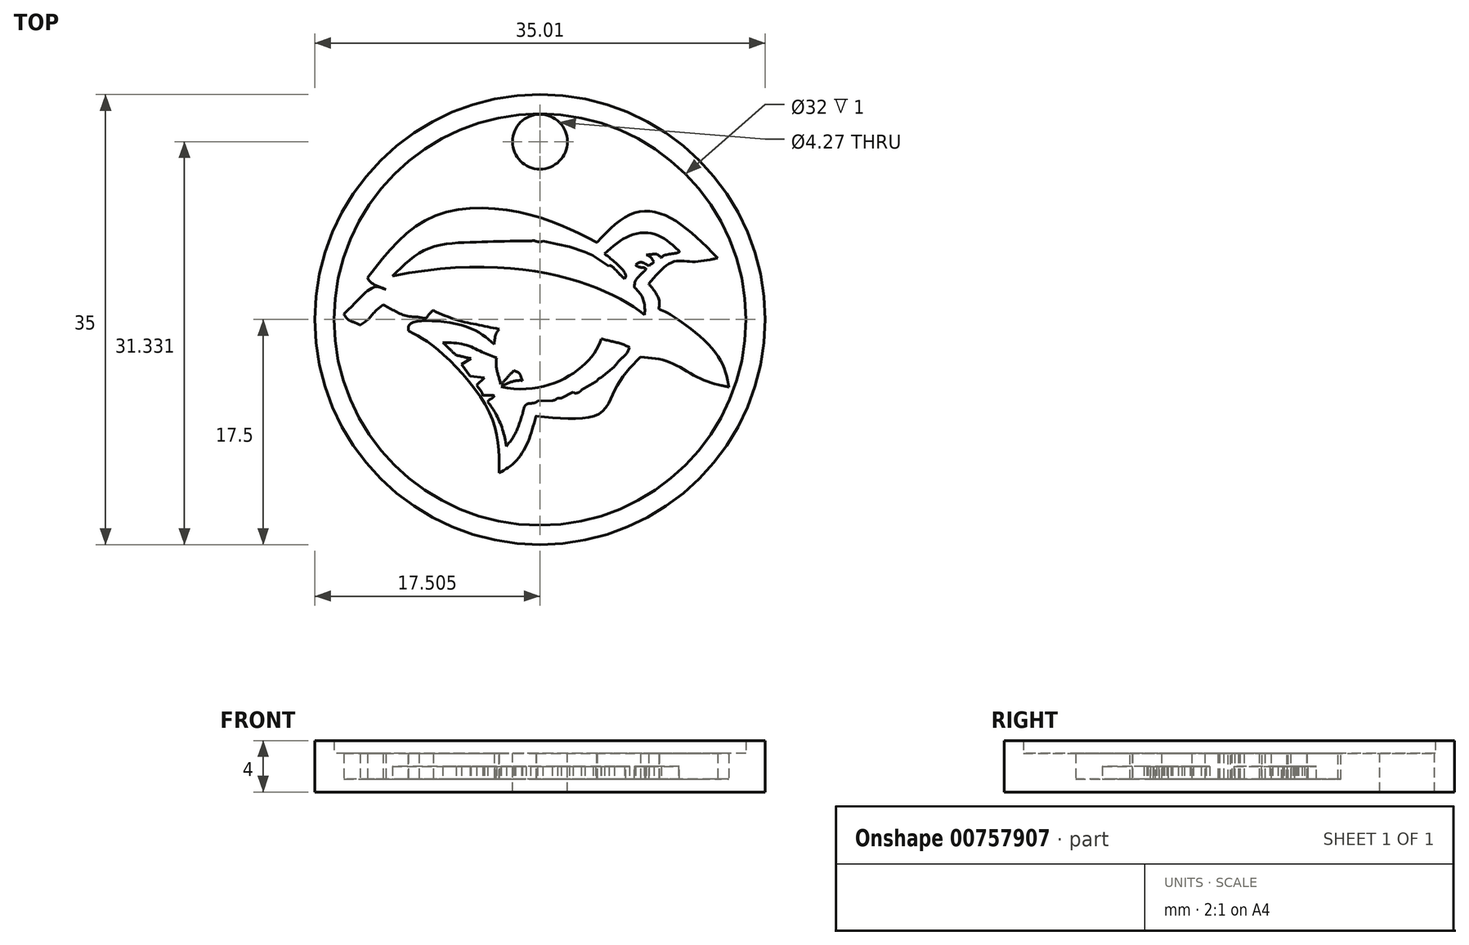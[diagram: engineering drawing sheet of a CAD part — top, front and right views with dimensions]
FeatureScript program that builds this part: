
annotation { "Feature Type Name" : "Feature", "Feature Type Description" : "" }
export const myFeature = defineFeature(function(context is Context, id is Id, definition is map)
    precondition{}
    {
        {
            var Q0;
            Q0=qCreatedBy(makeId("Top.planeOp"),FACE);
            var sketch = newSketch(context, id + "F0", { "sketchPlane" : qUnion([Q0])});
            skFitSpline(sketch, "E0", {"points": [v(1.9, -11.18) * mm, v(19.73, -8.42) * mm], "startDerivative": vector(15.68, 14.44) * mm, "endDerivative": vector(15.49, -6.43) * mm});
            skFitSpline(sketch, "E1", {"points": [v(19.73, -8.42) * mm, v(29.13, -9.64) * mm], "startDerivative": vector(8.75, 6.87) * mm, "endDerivative": vector(11.03, -9.35) * mm});
            skFitSpline(sketch, "E2", {"points": [v(29.13, -9.64) * mm, v(23.76, -11.66) * mm], "startDerivative": vector(-5.82, -0.85) * mm, "endDerivative": vector(-5.7, -5.15) * mm});
            skFitSpline(sketch, "E3", {"points": [v(23.76, -11.66) * mm, v(24.55, -13.61) * mm], "startDerivative": vector(0.88, -1.03) * mm, "endDerivative": vector(0, -2.22) * mm});
            skFitSpline(sketch, "E4", {"points": [v(24.55, -13.61) * mm, v(30, -19.69) * mm], "startDerivative": vector(2.55, -1.23) * mm, "endDerivative": vector(3.23, -8.18) * mm});
            skFitSpline(sketch, "E5", {"points": [v(30, -19.69) * mm, v(23.14, -17.33) * mm], "startDerivative": vector(-6.71, 1.98) * mm, "endDerivative": vector(-6.91, 1.31) * mm});
            skFitSpline(sketch, "E6", {"points": [v(23.14, -17.33) * mm, v(15, -21.93) * mm], "startDerivative": vector(-5.52, -6.77) * mm, "endDerivative": vector(-14.9, -0.63) * mm});
            skFitSpline(sketch, "E7", {"points": [v(1.9, -11.18) * mm, v(3.35, -12.11) * mm], "startDerivative": vector(1, -1.24) * mm, "endDerivative": vector(1.42, -0.66) * mm});
            skFitSpline(sketch, "E8", {"points": [v(3.35, -12.11) * mm, v(0.08, -14.01) * mm], "startDerivative": vector(-2.7, 0.63) * mm, "endDerivative": vector(-3.03, -3.02) * mm});
            skFitSpline(sketch, "E9", {"points": [v(0.08, -14.01) * mm, v(1.36, -14.87) * mm], "startDerivative": vector(1.17, -1.4) * mm, "endDerivative": vector(1.26, -0.62) * mm});
            skFitSpline(sketch, "E10", {"points": [v(1.36, -14.87) * mm, v(3.14, -13.28) * mm], "startDerivative": vector(2.06, 1.6) * mm, "endDerivative": vector(1.79, 1.42) * mm});
            skFitSpline(sketch, "E11", {"points": [v(3.14, -13.28) * mm, v(5.92, -14.25) * mm], "startDerivative": vector(2.61, -1.42) * mm, "endDerivative": vector(3, -0.33) * mm});
            skFitSpline(sketch, "E12", {"points": [v(5.92, -14.25) * mm, v(7.02, -13.73) * mm], "startDerivative": vector(1.6, -0.17) * mm, "endDerivative": vector(0.88, 0.76) * mm});
            skFitSpline(sketch, "E13", {"points": [v(7.02, -13.73) * mm, v(12.14, -15.18) * mm], "startDerivative": vector(5.39, -2.15) * mm, "endDerivative": vector(4.98, -1.03) * mm});
            skFitSpline(sketch, "E14", {"points": [v(12.14, -15.18) * mm, v(11.76, -16.34) * mm], "startDerivative": vector(-0.68, -1.03) * mm, "endDerivative": vector(-0.16, -1.26) * mm});
            skFitSpline(sketch, "E15", {"points": [v(15, -21.93) * mm, v(12.15, -26.36) * mm], "startDerivative": vector(-1.92, -6.19) * mm, "endDerivative": vector(-3.55, -2.43) * mm});
            skFitSpline(sketch, "E16", {"points": [v(11.76, -16.34) * mm, v(5.1, -15.31) * mm], "startDerivative": vector(-7.02, 4.21) * mm, "endDerivative": vector(-0.52, -1.73) * mm});
            skFitSpline(sketch, "E17", {"points": [v(5.1, -15.31) * mm, v(12.15, -26.36) * mm], "startDerivative": vector(6.41, -4.03) * mm, "endDerivative": vector(2.12, -13.78) * mm});
            skArc(sketch, "E18.filletArc", {"start": v(1.99, -11.1) * mm, "mid": v(1.95, -11.19) * mm, "end": v(1.98, -11.27) * mm});
            skArc(sketch, "E19.filletArc", {"start": v(3.08, -12.09) * mm, "mid": v(3.12, -12.05) * mm, "end": v(3.1, -12) * mm});
            skArc(sketch, "E20.filletArc", {"start": v(3.2, -13.31) * mm, "mid": v(3.14, -13.3) * mm, "end": v(3.09, -13.33) * mm});
            skArc(sketch, "E21.filletArc", {"start": v(0.14, -13.94) * mm, "mid": v(0.11, -14.01) * mm, "end": v(0.14, -14.08) * mm});
            skArc(sketch, "E22.filletArc", {"start": v(1.3, -14.84) * mm, "mid": v(1.36, -14.85) * mm, "end": v(1.4, -14.83) * mm});
            skArc(sketch, "E23.filletArc", {"start": v(5.19, -15.2) * mm, "mid": v(5.15, -15.29) * mm, "end": v(5.2, -15.37) * mm});
            skArc(sketch, "E24.filletArc", {"start": v(12.12, -26.2) * mm, "mid": v(12.18, -26.28) * mm, "end": v(12.28, -26.27) * mm});
            skArc(sketch, "E25.filletArc", {"start": v(15.07, -21.92) * mm, "mid": v(15.01, -21.94) * mm, "end": v(14.98, -22) * mm});
            skArc(sketch, "E26.filletArc", {"start": v(23.2, -17.35) * mm, "mid": v(23.15, -17.35) * mm, "end": v(23.1, -17.38) * mm});
            skArc(sketch, "E27.filletArc", {"start": v(29.8, -19.63) * mm, "mid": v(29.9, -19.6) * mm, "end": v(29.92, -19.49) * mm});
            skArc(sketch, "E28.filletArc", {"start": v(24.55, -13.55) * mm, "mid": v(24.57, -13.6) * mm, "end": v(24.6, -13.64) * mm});
            skArc(sketch, "E29.filletArc", {"start": v(23.83, -11.6) * mm, "mid": v(23.8, -11.66) * mm, "end": v(23.82, -11.73) * mm});
            skArc(sketch, "E30.filletArc", {"start": v(28.9, -9.68) * mm, "mid": v(28.99, -9.6) * mm, "end": v(28.96, -9.5) * mm});
            skArc(sketch, "E31.filletArc", {"start": v(19.67, -8.4) * mm, "mid": v(19.72, -8.4) * mm, "end": v(19.77, -8.39) * mm});
            skFitSpline(sketch, "E32.0", {"points": [v(22.75, -17.02) * mm, v(22.29, -17.59) * mm, v(21.44, -18.7) * mm, v(20.04, -20.05) * mm, v(18.13, -21.04) * mm, v(16.19, -21.38) * mm, v(14.98, -21.43) * mm]});
            skArc(sketch, "E32.1", {"start": v(23.3, -16.85) * mm, "mid": v(22.98, -16.88) * mm, "end": v(22.71, -17.07) * mm});
            skFitSpline(sketch, "E32.2", {"points": [v(30.14, -19.2) * mm, v(29.06, -18.89) * mm, v(26.8, -17.94) * mm, v(24.44, -17.07) * mm, v(23.23, -16.84) * mm]});
            skFitSpline(sketch, "E32.3", {"points": [v(24.33, -14.06) * mm, v(24.37, -14.08) * mm, v(24.47, -14.13) * mm, v(24.77, -14.33) * mm, v(25.27, -14.71) * mm, v(26.02, -15.34) * mm, v(27.1, -16.37) * mm, v(28.5, -17.92) * mm, v(29.29, -19.25) * mm, v(29.53, -19.87) * mm]});
            skArc(sketch, "E32.4", {"start": v(24.05, -13.57) * mm, "mid": v(24.14, -13.87) * mm, "end": v(24.37, -14.08) * mm});
            skFitSpline(sketch, "E32.5", {"points": [v(20.04, -8.82) * mm, v(20.73, -8.27) * mm, v(21.74, -7.72) * mm, v(23.06, -7.44) * mm, v(24.07, -7.46) * mm, v(25.14, -7.72) * mm, v(26.65, -8.38) * mm, v(27.9, -9.26) * mm, v(28.8, -10.03) * mm]});
            skFitSpline(sketch, "E32.6", {"points": [v(29.06, -9.15) * mm, v(28.58, -9.22) * mm, v(27.66, -9.33) * mm, v(26.3, -9.59) * mm, v(24.9, -10.15) * mm, v(23.93, -10.84) * mm, v(23.43, -11.3) * mm]});
            skArc(sketch, "E32.7", {"start": v(23.5, -11.22) * mm, "mid": v(23.3, -11.62) * mm, "end": v(23.43, -12.04) * mm});
            skFitSpline(sketch, "E32.8", {"points": [v(23.38, -11.99) * mm, v(23.43, -12.05) * mm, v(23.58, -12.25) * mm, v(23.82, -12.69) * mm, v(24, -13.18) * mm, v(24.05, -13.48) * mm, v(24.05, -13.61) * mm]});
            skFitSpline(sketch, "E33", {"points": [v(12.44, -25.45) * mm, v(14.54, -21.9) * mm], "startDerivative": vector(2.73, 2.38) * mm, "endDerivative": vector(1.4, 4.03) * mm});
            skFitSpline(sketch, "E34", {"points": [v(14.54, -21.9) * mm, v(15.05, -21.42) * mm], "startDerivative": vector(0.26, 1.18) * mm, "endDerivative": vector(0.95, 0.12) * mm});
            skFitSpline(sketch, "E35", {"points": [v(12.44, -25.45) * mm, v(6.55, -15.62) * mm], "startDerivative": vector(-2.37, 13.6) * mm, "endDerivative": vector(-8.28, 7.99) * mm});
            skFitSpline(sketch, "E36", {"points": [v(6.55, -15.62) * mm, v(12.05, -16.99) * mm], "startDerivative": vector(5.88, -0.05) * mm, "endDerivative": vector(5.45, -2.23) * mm});
            skFitSpline(sketch, "E37", {"points": [v(12.05, -16.99) * mm, v(12.95, -14.92) * mm], "startDerivative": vector(0.52, 2.46) * mm, "endDerivative": vector(1.23, 1.83) * mm});
            skFitSpline(sketch, "E38", {"points": [v(12.95, -14.92) * mm, v(6.91, -13.18) * mm], "startDerivative": vector(-5.93, 1.55) * mm, "endDerivative": vector(-6.7, 2.9) * mm});
            skFitSpline(sketch, "E39", {"points": [v(6.91, -13.18) * mm, v(5.98, -13.73) * mm], "startDerivative": vector(-0.93, -0.53) * mm, "endDerivative": vector(-1.23, -0.09) * mm});
            skFitSpline(sketch, "E40", {"points": [v(5.98, -13.73) * mm, v(3.28, -12.92) * mm], "startDerivative": vector(-3.4, 0.14) * mm, "endDerivative": vector(-1.02, 0.03) * mm});
            skFitSpline(sketch, "E41", {"points": [v(3.28, -12.92) * mm, v(1.34, -14.34) * mm], "startDerivative": vector(-1.4, 0.15) * mm, "endDerivative": vector(-1.9, -2) * mm});
            skFitSpline(sketch, "E42", {"points": [v(1.34, -14.34) * mm, v(0.74, -14.01) * mm], "startDerivative": vector(-0.78, 0.15) * mm, "endDerivative": vector(-0.43, 0.54) * mm});
            skFitSpline(sketch, "E43", {"points": [v(0.74, -14.01) * mm, v(2.56, -12.65) * mm], "startDerivative": vector(1.73, 1.92) * mm, "endDerivative": vector(2.06, 0.85) * mm});
            skFitSpline(sketch, "E44", {"points": [v(2.56, -12.65) * mm, v(3.62, -12.65) * mm], "startDerivative": vector(0.85, 0.31) * mm, "endDerivative": vector(1.28, -0.65) * mm});
            skFitSpline(sketch, "E45", {"points": [v(3.62, -12.65) * mm, v(5.48, -13.28) * mm], "startDerivative": vector(1.86, -0.85) * mm, "endDerivative": vector(2.3, -0.38) * mm});
            skFitSpline(sketch, "E46", {"points": [v(5.48, -13.28) * mm, v(6.16, -12.88) * mm], "startDerivative": vector(0.54, -0.16) * mm, "endDerivative": vector(0.18, 0.77) * mm});
            skFitSpline(sketch, "E47", {"points": [v(6.16, -12.88) * mm, v(2.68, -11.19) * mm], "startDerivative": vector(-3.39, 1.5) * mm, "endDerivative": vector(-3.44, 2.18) * mm});
            skFitSpline(sketch, "E48", {"points": [v(2.68, -11.19) * mm, v(19.77, -8.96) * mm], "startDerivative": vector(11.22, 9.9) * mm, "endDerivative": vector(19.56, -7.5) * mm});
            skFitSpline(sketch, "E49", {"points": [v(19.77, -8.96) * mm, v(20.08, -8.78) * mm], "startDerivative": vector(0.3, 0.18) * mm, "endDerivative": vector(0.3, 0.18) * mm});
            skSolve(sketch);
        }
        {
            var Q0;
            Q0=qCreatedBy(makeId("Top.planeOp"),FACE);
            var sketch = newSketch(context, id + "F1", { "sketchPlane" : qUnion([Q0])});
            skFitSpline(sketch, "E50.0.0", {"points": [v(24.05, -13.61) * mm, v(24.05, -13.48) * mm, v(24, -13.18) * mm, v(23.82, -12.69) * mm, v(23.58, -12.25) * mm, v(23.43, -12.05) * mm, v(23.38, -11.99) * mm]});
            skArc(sketch, "E50.0.1", {"start": v(23.43, -12.04) * mm, "mid": v(23.3, -11.62) * mm, "end": v(23.5, -11.22) * mm});
            skFitSpline(sketch, "E50.0.2", {"points": [v(23.43, -11.3) * mm, v(23.93, -10.84) * mm, v(24.9, -10.15) * mm, v(26.3, -9.59) * mm, v(27.66, -9.33) * mm, v(28.58, -9.22) * mm, v(29.06, -9.15) * mm]});
            skFitSpline(sketch, "E50.0.3", {"points": [v(28.8, -10.03) * mm, v(27.9, -9.26) * mm, v(26.65, -8.38) * mm, v(25.14, -7.72) * mm, v(24.07, -7.46) * mm, v(23.06, -7.44) * mm, v(21.74, -7.72) * mm, v(20.73, -8.27) * mm, v(20.04, -8.82) * mm]});
            skFitSpline(sketch, "E50.0.4", {"points": [v(20.08, -8.78) * mm, v(19.98, -8.84) * mm, v(19.87, -8.9) * mm, v(19.77, -8.96) * mm]});
            skFitSpline(sketch, "E50.0.5", {"points": [v(19.77, -8.96) * mm, v(13.25, -6.46) * mm, v(6.42, -7.89) * mm, v(2.68, -11.19) * mm]});
            skFitSpline(sketch, "E50.0.6", {"points": [v(2.68, -11.19) * mm, v(3.83, -11.91) * mm, v(5.03, -12.38) * mm, v(6.16, -12.88) * mm]});
            skFitSpline(sketch, "E50.0.7", {"points": [v(6.16, -12.88) * mm, v(6.1, -13.14) * mm, v(5.66, -13.34) * mm, v(5.48, -13.28) * mm]});
            skFitSpline(sketch, "E50.0.8", {"points": [v(5.48, -13.28) * mm, v(4.71, -13.16) * mm, v(4.24, -12.94) * mm, v(3.62, -12.65) * mm]});
            skFitSpline(sketch, "E50.0.9", {"points": [v(3.62, -12.65) * mm, v(3.2, -12.44) * mm, v(2.85, -12.55) * mm, v(2.56, -12.65) * mm]});
            skFitSpline(sketch, "E50.0.10", {"points": [v(2.56, -12.65) * mm, v(1.88, -12.94) * mm, v(1.32, -13.37) * mm, v(0.74, -14.01) * mm]});
            skFitSpline(sketch, "E50.0.11", {"points": [v(0.74, -14.01) * mm, v(0.89, -14.2) * mm, v(1.08, -14.29) * mm, v(1.34, -14.34) * mm]});
            skFitSpline(sketch, "E50.0.12", {"points": [v(1.34, -14.34) * mm, v(1.97, -13.68) * mm, v(2.81, -12.87) * mm, v(3.28, -12.92) * mm]});
            skFitSpline(sketch, "E50.0.13", {"points": [v(3.28, -12.92) * mm, v(3.62, -12.93) * mm, v(4.84, -13.69) * mm, v(5.98, -13.73) * mm]});
            skFitSpline(sketch, "E50.0.14", {"points": [v(5.98, -13.73) * mm, v(6.38, -13.7) * mm, v(6.6, -13.35) * mm, v(6.91, -13.18) * mm]});
            skFitSpline(sketch, "E50.0.15", {"points": [v(6.91, -13.18) * mm, v(9.14, -14.14) * mm, v(10.97, -14.4) * mm, v(12.95, -14.92) * mm]});
            skFitSpline(sketch, "E50.0.16", {"points": [v(12.95, -14.92) * mm, v(12.54, -15.53) * mm, v(12.22, -16.17) * mm, v(12.05, -16.99) * mm]});
            skFitSpline(sketch, "E50.0.17", {"points": [v(12.05, -16.99) * mm, v(10.23, -16.24) * mm, v(8.51, -15.64) * mm, v(6.55, -15.62) * mm]});
            skFitSpline(sketch, "E50.0.18", {"points": [v(6.55, -15.62) * mm, v(9.31, -18.29) * mm, v(11.65, -20.91) * mm, v(12.44, -25.45) * mm]});
            skFitSpline(sketch, "E50.0.19", {"points": [v(12.44, -25.45) * mm, v(13.35, -24.65) * mm, v(14.07, -23.24) * mm, v(14.54, -21.9) * mm]});
            skFitSpline(sketch, "E50.0.20", {"points": [v(14.54, -21.9) * mm, v(14.62, -21.5) * mm, v(14.73, -21.46) * mm, v(15.05, -21.42) * mm]});
            skFitSpline(sketch, "E50.0.21", {"points": [v(14.98, -21.43) * mm, v(16.19, -21.38) * mm, v(18.13, -21.04) * mm, v(20.04, -20.05) * mm, v(21.44, -18.7) * mm, v(22.29, -17.59) * mm, v(22.75, -17.02) * mm]});
            skArc(sketch, "E50.0.22", {"start": v(22.71, -17.07) * mm, "mid": v(22.98, -16.88) * mm, "end": v(23.3, -16.85) * mm});
            skFitSpline(sketch, "E50.0.23", {"points": [v(23.23, -16.84) * mm, v(24.44, -17.07) * mm, v(26.8, -17.94) * mm, v(29.06, -18.89) * mm, v(30.14, -19.2) * mm]});
            skFitSpline(sketch, "E50.0.24", {"points": [v(29.53, -19.87) * mm, v(29.29, -19.25) * mm, v(28.5, -17.92) * mm, v(27.1, -16.37) * mm, v(26.02, -15.34) * mm, v(25.27, -14.71) * mm, v(24.77, -14.33) * mm, v(24.47, -14.13) * mm, v(24.37, -14.08) * mm, v(24.33, -14.06) * mm]});
            skArc(sketch, "E50.0.25", {"start": v(24.37, -14.08) * mm, "mid": v(24.14, -13.87) * mm, "end": v(24.05, -13.57) * mm});
            skFitSpline(sketch, "E51", {"points": [v(3.84, -11.04) * mm, v(13.41, -8.32) * mm], "startDerivative": vector(8.23, 6.32) * mm, "endDerivative": vector(9.89, 0.28) * mm});
            skFitSpline(sketch, "E52", {"points": [v(13.41, -8.32) * mm, v(13.7, -12.02) * mm], "startDerivative": vector(1.93, -3.68) * mm, "endDerivative": vector(-0.86, -3.63) * mm});
            skFitSpline(sketch, "E53", {"points": [v(13.7, -12.02) * mm, v(14.59, -8.32) * mm], "startDerivative": vector(2.91, 3.23) * mm, "endDerivative": vector(-0.26, 4) * mm});
            skFitSpline(sketch, "E54", {"points": [v(14.59, -8.32) * mm, v(15.53, -8.33) * mm], "startDerivative": vector(0.94, 0.02) * mm, "endDerivative": vector(0.89, 0.22) * mm});
            skFitSpline(sketch, "E55", {"points": [v(15.53, -8.33) * mm, v(14.73, -12.66) * mm], "startDerivative": vector(1.01, -5.43) * mm, "endDerivative": vector(-2.55, -3.56) * mm});
            skFitSpline(sketch, "E56", {"points": [v(14.73, -12.66) * mm, v(16.7, -8.59) * mm], "startDerivative": vector(4.06, 2.07) * mm, "endDerivative": vector(-0.58, 5.5) * mm});
            skFitSpline(sketch, "E57", {"points": [v(16.7, -8.59) * mm, v(17.6, -8.77) * mm], "startDerivative": vector(0.9, -0.18) * mm, "endDerivative": vector(0.9, -0.18) * mm});
            skFitSpline(sketch, "E58", {"points": [v(17.6, -8.77) * mm, v(16.43, -13.05) * mm], "startDerivative": vector(0.72, -5.62) * mm, "endDerivative": vector(-2.94, -2.74) * mm});
            skFitSpline(sketch, "E59", {"points": [v(16.43, -13.05) * mm, v(18.8, -9.17) * mm], "startDerivative": vector(1.57, 0.05) * mm, "endDerivative": vector(0.27, 7.72) * mm});
            skFitSpline(sketch, "E60", {"points": [v(18.8, -9.17) * mm, v(19.44, -9.45) * mm], "startDerivative": vector(0.6, -0.28) * mm, "endDerivative": vector(0.6, -0.28) * mm});
            skFitSpline(sketch, "E61", {"points": [v(19.44, -9.45) * mm, v(17.95, -13.41) * mm], "startDerivative": vector(0.5, -5.93) * mm, "endDerivative": vector(-2.6, -2.56) * mm});
            skFitSpline(sketch, "E62", {"points": [v(17.95, -13.41) * mm, v(20.69, -10.28) * mm], "startDerivative": vector(2.8, 0.45) * mm, "endDerivative": vector(1.19, 4.82) * mm});
            skFitSpline(sketch, "E63", {"points": [v(20.69, -10.28) * mm, v(21.9, -11.26) * mm], "startDerivative": vector(0.39, 0.12) * mm, "endDerivative": vector(1.14, -1.05) * mm});
            skFitSpline(sketch, "E64", {"points": [v(21.9, -11.26) * mm, v(20.33, -9.31) * mm], "startDerivative": vector(0.2, 1.05) * mm, "endDerivative": vector(-1.84, 1.45) * mm});
            skFitSpline(sketch, "E65", {"points": [v(20.33, -9.31) * mm, v(26.08, -9.05) * mm], "startDerivative": vector(5.97, 4.25) * mm, "endDerivative": vector(5.3, -3.7) * mm});
            skFitSpline(sketch, "E66", {"points": [v(26.08, -9.05) * mm, v(24.74, -9.63) * mm], "startDerivative": vector(0.17, -0.39) * mm, "endDerivative": vector(-0.93, -0.65) * mm});
            skFitSpline(sketch, "E67", {"points": [v(24.74, -9.63) * mm, v(23.58, -9.4) * mm], "startDerivative": vector(-1.04, 0.84) * mm, "endDerivative": vector(-1.32, -0.14) * mm});
            skFitSpline(sketch, "E68", {"points": [v(23.58, -9.4) * mm, v(24.17, -9.95) * mm], "startDerivative": vector(0.92, -0.43) * mm, "endDerivative": vector(0.39, -0.6) * mm});
            skFitSpline(sketch, "E69", {"points": [v(24.17, -9.95) * mm, v(23.8, -10.25) * mm], "startDerivative": vector(-0.36, -0.35) * mm, "endDerivative": vector(-0.36, -0.35) * mm});
            skFitSpline(sketch, "E70", {"points": [v(23.8, -10.25) * mm, v(22.75, -10.16) * mm], "startDerivative": vector(-0.86, 0.44) * mm, "endDerivative": vector(-1.2, -0.56) * mm});
            skFitSpline(sketch, "E71", {"points": [v(22.75, -10.16) * mm, v(23.43, -10.65) * mm], "startDerivative": vector(0.59, -0.5) * mm, "endDerivative": vector(-0.34, -0.58) * mm});
            skFitSpline(sketch, "E72", {"points": [v(23.43, -10.65) * mm, v(22.66, -11.94) * mm], "startDerivative": vector(-1.1, -1.07) * mm, "endDerivative": vector(-0.18, -1.5) * mm});
            skFitSpline(sketch, "E73", {"points": [v(22.66, -11.94) * mm, v(23.45, -14.06) * mm], "startDerivative": vector(1.51, -1.7) * mm, "endDerivative": vector(0.03, -2.2) * mm});
            skFitSpline(sketch, "E74", {"points": [v(23.45, -14.06) * mm, v(27.16, -17.42) * mm], "startDerivative": vector(6.29, -4.19) * mm, "endDerivative": vector(1.38, -1.87) * mm});
            skFitSpline(sketch, "E75", {"points": [v(27.16, -17.42) * mm, v(20.07, -15.93) * mm], "startDerivative": vector(-8.04, 3.14) * mm, "endDerivative": vector(-4.68, -0.17) * mm});
            skFitSpline(sketch, "E76", {"points": [v(20.07, -15.93) * mm, v(22.29, -16.6) * mm], "startDerivative": vector(2.36, -0.56) * mm, "endDerivative": vector(1.91, -0.83) * mm});
            skFitSpline(sketch, "E77", {"points": [v(22.29, -16.6) * mm, v(21.1, -18.11) * mm], "startDerivative": vector(-0.92, -1.65) * mm, "endDerivative": vector(-1.2, -1.51) * mm});
            skFitSpline(sketch, "E78", {"points": [v(21.1, -18.11) * mm, v(18.95, -17) * mm], "startDerivative": vector(-3.4, 0.17) * mm, "endDerivative": vector(-1.62, 1.2) * mm});
            skFitSpline(sketch, "E79", {"points": [v(18.95, -17) * mm, v(20.06, -18.96) * mm], "startDerivative": vector(0.81, -1.7) * mm, "endDerivative": vector(1.69, -1.42) * mm});
            skFitSpline(sketch, "E80", {"points": [v(20.06, -18.96) * mm, v(19.65, -19.28) * mm], "startDerivative": vector(-0.59, -0.23) * mm, "endDerivative": vector(-0.42, -0.32) * mm});
            skFitSpline(sketch, "E81", {"points": [v(19.65, -19.28) * mm, v(17.88, -17.76) * mm], "startDerivative": vector(-3.11, 1.26) * mm, "endDerivative": vector(-1.35, 1.42) * mm});
            skFitSpline(sketch, "E82", {"points": [v(17.88, -17.76) * mm, v(18.54, -19.9) * mm], "startDerivative": vector(0.2, -2.76) * mm, "endDerivative": vector(0.75, -1.46) * mm});
            skFitSpline(sketch, "E83", {"points": [v(18.54, -19.9) * mm, v(17.88, -20.07) * mm], "startDerivative": vector(-0.4, -0.42) * mm, "endDerivative": vector(-0.66, 0.26) * mm});
            skFitSpline(sketch, "E84", {"points": [v(17.88, -20.07) * mm, v(16.54, -18.05) * mm], "startDerivative": vector(-1.6, 1.17) * mm, "endDerivative": vector(-1.15, 1.98) * mm});
            skFitSpline(sketch, "E85", {"points": [v(16.54, -18.05) * mm, v(16.98, -20.56) * mm], "startDerivative": vector(0.15, -2.54) * mm, "endDerivative": vector(0.5, -0.61) * mm});
            skFitSpline(sketch, "E86", {"points": [v(16.98, -20.56) * mm, v(16.26, -20.73) * mm], "startDerivative": vector(-0.73, 0.06) * mm, "endDerivative": vector(-0.71, -0.17) * mm});
            skFitSpline(sketch, "E87", {"points": [v(16.26, -20.73) * mm, v(15.15, -18.8) * mm], "startDerivative": vector(-2.14, 1.46) * mm, "endDerivative": vector(-0.77, 2.17) * mm});
            skFitSpline(sketch, "E88", {"points": [v(15.15, -18.8) * mm, v(15.13, -20.77) * mm], "startDerivative": vector(-1.07, -2.42) * mm, "endDerivative": vector(0.86, -1.36) * mm});
            skFitSpline(sketch, "E89", {"points": [v(15.13, -20.77) * mm, v(14.25, -21.06) * mm], "startDerivative": vector(-0.76, -0.44) * mm, "endDerivative": vector(-0.26, -0.22) * mm});
            skFitSpline(sketch, "E90", {"points": [v(14.25, -21.06) * mm, v(13.9, -21.96) * mm], "startDerivative": vector(-0.35, -0.28) * mm, "endDerivative": vector(-0.22, -0.57) * mm});
            skFitSpline(sketch, "E91", {"points": [v(11.26, -20.83) * mm, v(11.78, -20.35) * mm], "startDerivative": vector(0.48, 0.56) * mm, "endDerivative": vector(0.48, 0.56) * mm});
            skFitSpline(sketch, "E92", {"points": [v(11.78, -20.35) * mm, v(10.86, -20.3) * mm], "startDerivative": vector(-0.89, 0.08) * mm, "endDerivative": vector(-0.89, 0.08) * mm});
            skFitSpline(sketch, "E93", {"points": [v(10.86, -20.3) * mm, v(10.41, -19.52) * mm], "startDerivative": vector(-0.33, 0.9) * mm, "endDerivative": vector(-0.44, 0.68) * mm});
            skFitSpline(sketch, "E94", {"points": [v(10.41, -19.52) * mm, v(11, -18.96) * mm], "startDerivative": vector(0.58, 0.56) * mm, "endDerivative": vector(0.58, 0.56) * mm});
            skFitSpline(sketch, "E95", {"points": [v(11, -18.96) * mm, v(9.88, -18.84) * mm], "startDerivative": vector(-1.1, 0.12) * mm, "endDerivative": vector(-1.1, 0.12) * mm});
            skFitSpline(sketch, "E96", {"points": [v(9.88, -18.84) * mm, v(9.21, -17.92) * mm], "startDerivative": vector(-0.67, 0.92) * mm, "endDerivative": vector(-0.67, 0.92) * mm});
            skFitSpline(sketch, "E97", {"points": [v(9.21, -17.92) * mm, v(9.96, -17.46) * mm], "startDerivative": vector(0.74, 0.46) * mm, "endDerivative": vector(0.74, 0.46) * mm});
            skFitSpline(sketch, "E98", {"points": [v(9.96, -17.46) * mm, v(8.81, -17.22) * mm], "startDerivative": vector(-1.44, 0.28) * mm, "endDerivative": vector(-1.44, 0.28) * mm});
            skFitSpline(sketch, "E99", {"points": [v(8.81, -17.22) * mm, v(7.78, -16.22) * mm], "startDerivative": vector(-0.95, 0.9) * mm, "endDerivative": vector(-0.95, 0.9) * mm});
            skFitSpline(sketch, "E100", {"points": [v(7.78, -16.22) * mm, v(11.94, -17.4) * mm], "startDerivative": vector(5.16, -0.5) * mm, "endDerivative": vector(3.48, -1.4) * mm});
            skFitSpline(sketch, "E101", {"points": [v(11.94, -17.4) * mm, v(12.27, -19.48) * mm], "startDerivative": vector(0.03, -2.57) * mm, "endDerivative": vector(0.53, -1.97) * mm});
            skFitSpline(sketch, "E102", {"points": [v(12.27, -19.48) * mm, v(13.3, -18.4) * mm], "startDerivative": vector(1.01, 1.04) * mm, "endDerivative": vector(1.01, 1.04) * mm});
            skFitSpline(sketch, "E103", {"points": [v(13.3, -18.4) * mm, v(13.97, -19.17) * mm], "startDerivative": vector(1.34, -0.7) * mm, "endDerivative": vector(0.44, -0.97) * mm});
            skFitSpline(sketch, "E104", {"points": [v(13.97, -19.17) * mm, v(16.18, -17.04) * mm], "startDerivative": vector(3.84, 1.1) * mm, "endDerivative": vector(0.14, 3.15) * mm});
            skFitSpline(sketch, "E105", {"points": [v(16.18, -17.04) * mm, v(13.45, -14.6) * mm], "startDerivative": vector(-0.11, 3.94) * mm, "endDerivative": vector(-4.22, 0.7) * mm});
            skFitSpline(sketch, "E106", {"points": [v(13.45, -14.6) * mm, v(9, -13.38) * mm], "startDerivative": vector(-4.42, 1.25) * mm, "endDerivative": vector(-4.2, 1.62) * mm});
            skFitSpline(sketch, "E107", {"points": [v(9, -13.38) * mm, v(10.38, -12.66) * mm], "startDerivative": vector(1.58, 0.5) * mm, "endDerivative": vector(1.3, 0.93) * mm});
            skFitSpline(sketch, "E108", {"points": [v(10.38, -12.66) * mm, v(12.17, -13.47) * mm], "startDerivative": vector(0.75, -3.07) * mm, "endDerivative": vector(1.46, 0.74) * mm});
            skFitSpline(sketch, "E109", {"points": [v(12.17, -13.47) * mm, v(12.5, -13.49) * mm], "startDerivative": vector(0.47, 0.16) * mm, "endDerivative": vector(0.27, -0.32) * mm});
            skFitSpline(sketch, "E110", {"points": [v(12.5, -13.49) * mm, v(13.53, -14.39) * mm], "startDerivative": vector(0.33, -2.1) * mm, "endDerivative": vector(1.36, 0) * mm});
            skFitSpline(sketch, "E111", {"points": [v(13.53, -14.39) * mm, v(14.49, -13.99) * mm], "startDerivative": vector(1.08, -0.06) * mm, "endDerivative": vector(0.76, 0.87) * mm});
            skFitSpline(sketch, "E112", {"points": [v(14.49, -13.99) * mm, v(16.04, -14.1) * mm], "startDerivative": vector(2, 0.1) * mm, "endDerivative": vector(1.44, -0.46) * mm});
            skFitSpline(sketch, "E113", {"points": [v(16.04, -14.1) * mm, v(16.33, -15.15) * mm], "startDerivative": vector(0.74, -0.9) * mm, "endDerivative": vector(-0.07, -0.99) * mm});
            skFitSpline(sketch, "E114", {"points": [v(16.33, -15.15) * mm, v(18.94, -14.1) * mm], "startDerivative": vector(3.03, -0.07) * mm, "endDerivative": vector(2.89, 0.45) * mm});
            skFitSpline(sketch, "E115", {"points": [v(18.94, -14.1) * mm, v(19.76, -14.84) * mm], "startDerivative": vector(0.73, -0.46) * mm, "endDerivative": vector(0.72, -0.14) * mm});
            skFitSpline(sketch, "E116", {"points": [v(19.76, -14.84) * mm, v(21.12, -14.3) * mm], "startDerivative": vector(0.73, -0.16) * mm, "endDerivative": vector(1.3, 0.6) * mm});
            skFitSpline(sketch, "E117", {"points": [v(21.12, -14.3) * mm, v(20.7, -13.79) * mm], "startDerivative": vector(-0.24, 0.79) * mm, "endDerivative": vector(-0.37, 0.45) * mm});
            skFitSpline(sketch, "E118", {"points": [v(20.7, -13.79) * mm, v(19.7, -14.48) * mm], "startDerivative": vector(-0.74, -0.94) * mm, "endDerivative": vector(-0.24, 0.1) * mm});
            skFitSpline(sketch, "E119", {"points": [v(19.7, -14.48) * mm, v(18.92, -13.54) * mm], "startDerivative": vector(-0.74, 0.25) * mm, "endDerivative": vector(-0.25, -0.02) * mm});
            skFitSpline(sketch, "E120", {"points": [v(18.92, -13.54) * mm, v(16.55, -14.6) * mm], "startDerivative": vector(-0.84, 0.06) * mm, "endDerivative": vector(-0.6, 0.49) * mm});
            skFitSpline(sketch, "E121", {"points": [v(16.55, -14.6) * mm, v(16.18, -13.57) * mm], "startDerivative": vector(-0.3, 1.3) * mm, "endDerivative": vector(-0.47, 0.16) * mm});
            skFitSpline(sketch, "E122", {"points": [v(16.18, -13.57) * mm, v(14.5, -13.55) * mm], "startDerivative": vector(-1.55, 0.5) * mm, "endDerivative": vector(-1.68, 0.28) * mm});
            skFitSpline(sketch, "E123", {"points": [v(14.5, -13.55) * mm, v(13.5, -12.78) * mm], "startDerivative": vector(-0.53, 1.58) * mm, "endDerivative": vector(-1.25, 0.1) * mm});
            skFitSpline(sketch, "E124", {"points": [v(13.5, -12.78) * mm, v(12.56, -13) * mm], "startDerivative": vector(-1.25, -0.02) * mm, "endDerivative": vector(-0.54, -0.36) * mm});
            skFitSpline(sketch, "E125", {"points": [v(12.56, -13) * mm, v(11.5, -12.1) * mm], "startDerivative": vector(-0.9, 2.44) * mm, "endDerivative": vector(-1.24, 0.07) * mm});
            skFitSpline(sketch, "E126", {"points": [v(11.5, -12.1) * mm, v(11.98, -11.77) * mm], "startDerivative": vector(-0.39, 0.1) * mm, "endDerivative": vector(0.44, 0.35) * mm});
            skFitSpline(sketch, "E127", {"points": [v(11.98, -11.77) * mm, v(7.08, -12.67) * mm], "startDerivative": vector(-5.81, 0.44) * mm, "endDerivative": vector(-1.14, -2.35) * mm});
            skFitSpline(sketch, "E128", {"points": [v(7.08, -12.67) * mm, v(3.84, -11.04) * mm], "startDerivative": vector(-4.8, 1.52) * mm, "endDerivative": vector(-2.77, 1.86) * mm});
            skFitSpline(sketch, "E129", {"points": [v(12.55, -18.59) * mm, v(13.62, -15.14) * mm], "startDerivative": vector(-0.92, 3.25) * mm, "endDerivative": vector(1.86, 0.61) * mm});
            skFitSpline(sketch, "E130", {"points": [v(13.62, -15.14) * mm, v(15.3, -16.09) * mm, v(12.55, -18.59) * mm], "startDerivative": vector(3.4, 0.65) * mm, "endDerivative": vector(-9.16, -12.2) * mm});
            skFitSpline(sketch, "E131", {"points": [v(13.8, -18.02) * mm, v(15.5, -16.73) * mm], "startDerivative": vector(0.1, 0.98) * mm, "endDerivative": vector(0.5, -0.27) * mm});
            skFitSpline(sketch, "E132", {"points": [v(15.5, -16.73) * mm, v(14.53, -18.5) * mm, v(13.8, -18.02) * mm], "startDerivative": vector(1.51, -3.13) * mm, "endDerivative": vector(-1.63, 2.58) * mm});
            skFitSpline(sketch, "E133", {"points": [v(12.77, -13.51) * mm, v(13.01, -13.16) * mm], "startDerivative": vector(-0.22, 0.45) * mm, "endDerivative": vector(0.64, -0.03) * mm});
            skFitSpline(sketch, "E134", {"points": [v(13.01, -13.16) * mm, v(14.04, -13.47) * mm], "startDerivative": vector(1.02, 0.03) * mm, "endDerivative": vector(0.74, -0.9) * mm});
            skFitSpline(sketch, "E135", {"points": [v(14.04, -13.47) * mm, v(13.94, -13.93) * mm], "startDerivative": vector(0.3, -0.38) * mm, "endDerivative": vector(-0.63, -0.37) * mm});
            skFitSpline(sketch, "E136", {"points": [v(13.94, -13.93) * mm, v(12.77, -13.51) * mm], "startDerivative": vector(-0.59, -0.4) * mm, "endDerivative": vector(-1.22, 2) * mm});
            skFitSpline(sketch, "E137", {"points": [v(11.9, -13.25) * mm, v(10.88, -12.86) * mm], "startDerivative": vector(-1, -0.24) * mm, "endDerivative": vector(-0.89, 1.15) * mm});
            skFitSpline(sketch, "E138", {"points": [v(10.88, -12.86) * mm, v(11.21, -12.4) * mm], "startDerivative": vector(-0.4, 0.49) * mm, "endDerivative": vector(1.09, 0) * mm});
            skFitSpline(sketch, "E139", {"points": [v(11.21, -12.4) * mm, v(12.02, -12.73) * mm], "startDerivative": vector(0.81, -0.06) * mm, "endDerivative": vector(0.72, -0.51) * mm});
            skFitSpline(sketch, "E140", {"points": [v(11.9, -13.25) * mm, v(12.02, -12.73) * mm], "startDerivative": vector(0.86, 0.31) * mm, "endDerivative": vector(-0.44, 0.3) * mm});
            skFitSpline(sketch, "E141", {"points": [v(7.78, -12.74) * mm, v(8.63, -13.15) * mm, v(8.93, -13.02) * mm, v(8.04, -12.67) * mm, v(7.78, -12.74) * mm]});
            skFitSpline(sketch, "E142", {"points": [v(8.68, -12.39) * mm, v(9.2, -12.88) * mm, v(9.72, -12.63) * mm, v(9.66, -12.52) * mm, v(9.16, -12.52) * mm, v(8.72, -12.3) * mm, v(8.68, -12.39) * mm]});
            skFitSpline(sketch, "E143", {"points": [v(9.66, -12.23) * mm, v(9.99, -12.44) * mm, v(10.39, -12.24) * mm, v(10, -12.14) * mm, v(9.66, -12.23) * mm]});
            skFitSpline(sketch, "E144", {"points": [v(11.26, -20.83) * mm, v(12.7, -24.28) * mm], "startDerivative": vector(1.77, -2.64) * mm, "endDerivative": vector(0.86, -3.83) * mm});
            skFitSpline(sketch, "E145", {"points": [v(12.7, -24.28) * mm, v(13.9, -21.96) * mm], "startDerivative": vector(1.54, 2.01) * mm, "endDerivative": vector(0.96, 2.82) * mm});
            skCircle(sketch, "E146", {"center": v(15.32, -14.43) * mm, "radius": 17.5 * mm});
            skFitSpline(sketch, "E147.0.0", {"points": [v(12.15, -26.36) * mm, v(13.33, -25.55) * mm, v(14.36, -23.99) * mm, v(15, -21.93) * mm]});
            skArc(sketch, "E147.0.1", {"start": v(14.98, -22) * mm, "mid": v(15.01, -21.94) * mm, "end": v(15.07, -21.92) * mm});
            skFitSpline(sketch, "E147.0.2", {"points": [v(15, -21.93) * mm, v(19.97, -21.72) * mm, v(21.3, -19.6) * mm, v(23.14, -17.33) * mm]});
            skArc(sketch, "E147.0.3", {"start": v(23.1, -17.38) * mm, "mid": v(23.15, -17.35) * mm, "end": v(23.2, -17.35) * mm});
            skFitSpline(sketch, "E147.0.4", {"points": [v(23.14, -17.33) * mm, v(25.44, -17.77) * mm, v(27.76, -19.03) * mm, v(30, -19.69) * mm]});
            skArc(sketch, "E147.0.5", {"start": v(29.8, -19.63) * mm, "mid": v(29.9, -19.6) * mm, "end": v(29.92, -19.49) * mm});
            skFitSpline(sketch, "E147.0.6", {"points": [v(30, -19.69) * mm, v(28.92, -16.96) * mm, v(25.4, -14.02) * mm, v(24.55, -13.61) * mm]});
            skArc(sketch, "E147.0.7", {"start": v(24.6, -13.64) * mm, "mid": v(24.57, -13.6) * mm, "end": v(24.55, -13.55) * mm});
            skFitSpline(sketch, "E147.0.8", {"points": [v(24.55, -13.61) * mm, v(24.55, -12.87) * mm, v(24.05, -12) * mm, v(23.76, -11.66) * mm]});
            skArc(sketch, "E147.0.9", {"start": v(23.82, -11.73) * mm, "mid": v(23.8, -11.66) * mm, "end": v(23.83, -11.6) * mm});
            skFitSpline(sketch, "E147.0.10", {"points": [v(23.76, -11.66) * mm, v(25.66, -9.94) * mm, v(27.19, -9.93) * mm, v(29.13, -9.64) * mm]});
            skArc(sketch, "E147.0.11", {"start": v(28.9, -9.68) * mm, "mid": v(28.99, -9.6) * mm, "end": v(28.96, -9.5) * mm});
            skFitSpline(sketch, "E147.0.12", {"points": [v(29.13, -9.64) * mm, v(25.45, -6.53) * mm, v(22.65, -6.14) * mm, v(19.73, -8.42) * mm]});
            skArc(sketch, "E147.0.13", {"start": v(19.77, -8.39) * mm, "mid": v(19.72, -8.4) * mm, "end": v(19.67, -8.4) * mm});
            skFitSpline(sketch, "E147.0.14", {"points": [v(19.73, -8.42) * mm, v(14.57, -6.28) * mm, v(7.13, -6.37) * mm, v(1.9, -11.18) * mm]});
            skArc(sketch, "E147.0.15", {"start": v(1.99, -11.1) * mm, "mid": v(1.95, -11.19) * mm, "end": v(1.98, -11.27) * mm});
            skFitSpline(sketch, "E147.0.16", {"points": [v(1.9, -11.18) * mm, v(2.24, -11.6) * mm, v(2.88, -11.9) * mm, v(3.35, -12.11) * mm]});
            skArc(sketch, "E147.0.17", {"start": v(3.1, -12) * mm, "mid": v(3.12, -12.05) * mm, "end": v(3.08, -12.09) * mm});
            skFitSpline(sketch, "E147.0.18", {"points": [v(3.35, -12.11) * mm, v(2.45, -11.9) * mm, v(1.09, -13) * mm, v(0.08, -14.01) * mm]});
            skArc(sketch, "E147.0.19", {"start": v(0.14, -13.94) * mm, "mid": v(0.11, -14.01) * mm, "end": v(0.14, -14.08) * mm});
            skFitSpline(sketch, "E147.0.20", {"points": [v(0.08, -14.01) * mm, v(0.47, -14.47) * mm, v(0.94, -14.66) * mm, v(1.36, -14.87) * mm]});
            skArc(sketch, "E147.0.21", {"start": v(1.3, -14.84) * mm, "mid": v(1.36, -14.85) * mm, "end": v(1.4, -14.83) * mm});
            skFitSpline(sketch, "E147.0.22", {"points": [v(1.36, -14.87) * mm, v(2.05, -14.34) * mm, v(2.55, -13.76) * mm, v(3.14, -13.28) * mm]});
            skArc(sketch, "E147.0.23", {"start": v(3.09, -13.33) * mm, "mid": v(3.14, -13.3) * mm, "end": v(3.2, -13.31) * mm});
            skFitSpline(sketch, "E147.0.24", {"points": [v(3.14, -13.28) * mm, v(4.01, -13.76) * mm, v(4.92, -14.14) * mm, v(5.92, -14.25) * mm]});
            skFitSpline(sketch, "E147.0.25", {"points": [v(5.92, -14.25) * mm, v(6.45, -14.3) * mm, v(6.73, -13.98) * mm, v(7.02, -13.73) * mm]});
            skFitSpline(sketch, "E147.0.26", {"points": [v(7.02, -13.73) * mm, v(8.82, -14.45) * mm, v(10.48, -14.83) * mm, v(12.14, -15.18) * mm]});
            skFitSpline(sketch, "E147.0.27", {"points": [v(12.14, -15.18) * mm, v(11.91, -15.52) * mm, v(11.81, -15.92) * mm, v(11.76, -16.34) * mm]});
            skFitSpline(sketch, "E147.0.28", {"points": [v(11.76, -16.34) * mm, v(9.42, -14.94) * mm, v(5.27, -14.73) * mm, v(5.1, -15.31) * mm]});
            skArc(sketch, "E147.0.29", {"start": v(5.19, -15.2) * mm, "mid": v(5.15, -15.29) * mm, "end": v(5.2, -15.37) * mm});
            skFitSpline(sketch, "E147.0.30", {"points": [v(5.1, -15.31) * mm, v(7.24, -16.65) * mm, v(11.44, -21.77) * mm, v(12.15, -26.36) * mm]});
            skArc(sketch, "E147.0.31", {"start": v(12.12, -26.2) * mm, "mid": v(12.18, -26.28) * mm, "end": v(12.28, -26.27) * mm});
            skSolve(sketch);
        }
        {
            var Q0;
            Q0=qCreatedBy(makeId("Top.planeOp"),FACE);
            var sketch = newSketch(context, id + "F2", { "sketchPlane" : qUnion([Q0])});
            skFitSpline(sketch, "E148.0", {"points": [v(11.26, -20.83) * mm, v(11.85, -21.7) * mm, v(12.42, -23) * mm, v(12.7, -24.28) * mm]});
            skFitSpline(sketch, "E149.0", {"points": [v(11.26, -20.83) * mm, v(11.42, -20.64) * mm, v(11.62, -20.53) * mm, v(11.78, -20.35) * mm]});
            skFitSpline(sketch, "E150.0", {"points": [v(11.78, -20.35) * mm, v(11.48, -20.32) * mm, v(11.16, -20.33) * mm, v(10.86, -20.3) * mm]});
            skFitSpline(sketch, "E151.0", {"points": [v(10.86, -20.3) * mm, v(10.75, -20) * mm, v(10.56, -19.75) * mm, v(10.41, -19.52) * mm]});
            skFitSpline(sketch, "E152.0", {"points": [v(10.41, -19.52) * mm, v(10.6, -19.33) * mm, v(10.8, -19.15) * mm, v(11, -18.96) * mm]});
            skFitSpline(sketch, "E153.0", {"points": [v(11, -18.96) * mm, v(10.62, -18.92) * mm, v(10.25, -18.88) * mm, v(9.88, -18.84) * mm]});
            skFitSpline(sketch, "E154.0", {"points": [v(9.88, -18.84) * mm, v(9.66, -18.54) * mm, v(9.44, -18.23) * mm, v(9.21, -17.92) * mm]});
            skFitSpline(sketch, "E155.0", {"points": [v(9.21, -17.92) * mm, v(9.46, -17.77) * mm, v(9.7, -17.61) * mm, v(9.96, -17.46) * mm]});
            skFitSpline(sketch, "E156.0", {"points": [v(8.81, -17.22) * mm, v(8.5, -16.92) * mm, v(8.1, -16.52) * mm, v(7.78, -16.22) * mm]});
            skFitSpline(sketch, "E157.0", {"points": [v(9.96, -17.46) * mm, v(9.48, -17.37) * mm, v(9.3, -17.3) * mm, v(8.81, -17.22) * mm]});
            skFitSpline(sketch, "E158.0", {"points": [v(7.78, -16.22) * mm, v(9.5, -16.39) * mm, v(10.78, -16.94) * mm, v(11.94, -17.4) * mm]});
            skFitSpline(sketch, "E159.0", {"points": [v(11.94, -17.4) * mm, v(11.95, -18.26) * mm, v(12.1, -18.82) * mm, v(12.27, -19.48) * mm]});
            skFitSpline(sketch, "E160.0", {"points": [v(13.3, -18.4) * mm, v(13.74, -18.63) * mm, v(13.82, -18.85) * mm, v(13.97, -19.17) * mm]});
            skFitSpline(sketch, "E161.0", {"points": [v(12.7, -24.28) * mm, v(13.22, -23.61) * mm, v(13.57, -22.9) * mm, v(13.9, -21.96) * mm]});
            skFitSpline(sketch, "E162.0", {"points": [v(14.25, -21.06) * mm, v(14.13, -21.15) * mm, v(13.97, -21.77) * mm, v(13.9, -21.96) * mm]});
            skFitSpline(sketch, "E163.0", {"points": [v(15.13, -20.77) * mm, v(14.88, -20.91) * mm, v(14.34, -20.99) * mm, v(14.25, -21.06) * mm]});
            skFitSpline(sketch, "E164.0", {"points": [v(16.98, -20.56) * mm, v(16.73, -20.54) * mm, v(16.5, -20.68) * mm, v(16.26, -20.73) * mm]});
            skFitSpline(sketch, "E165.0", {"points": [v(18.54, -19.9) * mm, v(18.4, -20.05) * mm, v(18.1, -20.16) * mm, v(17.88, -20.07) * mm]});
            skFitSpline(sketch, "E166.0", {"points": [v(20.06, -18.96) * mm, v(19.87, -19.04) * mm, v(19.78, -19.17) * mm, v(19.65, -19.28) * mm]});
            skFitSpline(sketch, "E167.0", {"points": [v(22.29, -16.6) * mm, v(21.98, -17.15) * mm, v(21.5, -17.6) * mm, v(21.1, -18.11) * mm]});
            skFitSpline(sketch, "E168.0", {"points": [v(20.07, -15.93) * mm, v(20.86, -16.11) * mm, v(21.65, -16.32) * mm, v(22.29, -16.6) * mm]});
            skFitSpline(sketch, "E169.0", {"points": [v(22.66, -11.94) * mm, v(23.17, -12.5) * mm, v(23.44, -13.32) * mm, v(23.45, -14.06) * mm]});
            skFitSpline(sketch, "E170.0", {"points": [v(23.43, -10.65) * mm, v(23.06, -11) * mm, v(22.72, -11.44) * mm, v(22.66, -11.94) * mm]});
            skFitSpline(sketch, "E171.0", {"points": [v(22.75, -10.16) * mm, v(22.94, -10.33) * mm, v(23.54, -10.46) * mm, v(23.43, -10.65) * mm]});
            skFitSpline(sketch, "E172.0", {"points": [v(22.75, -10.16) * mm, v(22.94, -10.33) * mm, v(23.54, -10.46) * mm, v(23.43, -10.65) * mm]});
            skFitSpline(sketch, "E173.0", {"points": [v(23.8, -10.25) * mm, v(23.51, -10.1) * mm, v(23.15, -9.98) * mm, v(22.75, -10.16) * mm]});
            skFitSpline(sketch, "E174.0", {"points": [v(24.17, -9.95) * mm, v(24.05, -10.07) * mm, v(23.92, -10.14) * mm, v(23.8, -10.25) * mm]});
            skFitSpline(sketch, "E175.0", {"points": [v(23.58, -9.4) * mm, v(23.88, -9.55) * mm, v(24.04, -9.75) * mm, v(24.17, -9.95) * mm]});
            skFitSpline(sketch, "E176.0", {"points": [v(24.74, -9.63) * mm, v(24.4, -9.35) * mm, v(24.02, -9.36) * mm, v(23.58, -9.4) * mm]});
            skFitSpline(sketch, "E177.0", {"points": [v(26.08, -9.05) * mm, v(26.14, -9.18) * mm, v(25.05, -9.41) * mm, v(24.74, -9.63) * mm]});
            skFitSpline(sketch, "E178.0", {"points": [v(20.33, -9.31) * mm, v(22.32, -7.9) * mm, v(24.31, -7.81) * mm, v(26.08, -9.05) * mm]});
            skFitSpline(sketch, "E179.0", {"points": [v(21.9, -11.26) * mm, v(21.96, -10.91) * mm, v(20.94, -9.8) * mm, v(20.33, -9.31) * mm]});
            skFitSpline(sketch, "E180.0", {"points": [v(20.69, -10.28) * mm, v(20.81, -10.24) * mm, v(21.52, -10.91) * mm, v(21.9, -11.26) * mm]});
            skFitSpline(sketch, "E181.0", {"points": [v(18.8, -9.17) * mm, v(19, -9.26) * mm, v(19.24, -9.36) * mm, v(19.44, -9.45) * mm]});
            skFitSpline(sketch, "E182.0", {"points": [v(16.7, -8.59) * mm, v(17, -8.65) * mm, v(17.3, -8.71) * mm, v(17.6, -8.77) * mm]});
            skFitSpline(sketch, "E183.0", {"points": [v(14.59, -8.32) * mm, v(14.9, -8.3) * mm, v(15.24, -8.4) * mm, v(15.53, -8.33) * mm]});
            skFitSpline(sketch, "E184.0", {"points": [v(3.84, -11.04) * mm, v(6.58, -8.94) * mm, v(10.12, -8.41) * mm, v(13.41, -8.32) * mm]});
            skFitSpline(sketch, "E185.0", {"points": [v(12.27, -19.48) * mm, v(12.6, -19.13) * mm, v(12.95, -18.74) * mm, v(13.3, -18.4) * mm]});
            skFitSpline(sketch, "E186", {"points": [v(13.97, -19.17) * mm, v(12.3, -19.65) * mm], "startDerivative": vector(-1.75, 0.19) * mm, "endDerivative": vector(-1.57, -0.91) * mm});
            skFitSpline(sketch, "E187", {"points": [v(12.3, -19.65) * mm, v(20.07, -15.93) * mm], "startDerivative": vector(11.46, -2.65) * mm, "endDerivative": vector(1.7, 6.36) * mm});
            skFitSpline(sketch, "E188", {"points": [v(15.13, -20.77) * mm, v(16.26, -20.73) * mm], "startDerivative": vector(1.13, 0.04) * mm, "endDerivative": vector(1.13, 0.04) * mm});
            skFitSpline(sketch, "E189", {"points": [v(16.98, -20.56) * mm, v(17.88, -20.07) * mm], "startDerivative": vector(0.9, 0.5) * mm, "endDerivative": vector(0.9, 0.5) * mm});
            skFitSpline(sketch, "E190", {"points": [v(18.54, -19.9) * mm, v(19.65, -19.28) * mm], "startDerivative": vector(1.11, 0.63) * mm, "endDerivative": vector(1.11, 0.63) * mm});
            skFitSpline(sketch, "E191", {"points": [v(20.06, -18.96) * mm, v(21.1, -18.11) * mm], "startDerivative": vector(1.03, 0.85) * mm, "endDerivative": vector(1.03, 0.85) * mm});
            skFitSpline(sketch, "E192", {"points": [v(23.45, -14.06) * mm, v(3.84, -11.04) * mm], "startDerivative": vector(-8.89, 6.95) * mm, "endDerivative": vector(-29.85, -6.02) * mm});
            skFitSpline(sketch, "E193", {"points": [v(13.41, -8.32) * mm, v(14.59, -8.32) * mm], "startDerivative": vector(1.18, 0) * mm, "endDerivative": vector(1.18, 0) * mm});
            skFitSpline(sketch, "E194", {"points": [v(15.53, -8.33) * mm, v(16.7, -8.59) * mm], "startDerivative": vector(1.16, -0.26) * mm, "endDerivative": vector(1.16, -0.26) * mm});
            skFitSpline(sketch, "E195", {"points": [v(17.6, -8.77) * mm, v(18.8, -9.17) * mm], "startDerivative": vector(1.2, -0.4) * mm, "endDerivative": vector(1.2, -0.4) * mm});
            skFitSpline(sketch, "E196", {"points": [v(19.44, -9.45) * mm, v(20.69, -10.28) * mm], "startDerivative": vector(1.25, -0.83) * mm, "endDerivative": vector(1.25, -0.83) * mm});
            skSolve(sketch);
        }
        {
            var Q0;
            Q0=qCreatedBy(makeId("Top.planeOp"),FACE);
            var sketch = newSketch(context, id + "F3", { "sketchPlane" : qUnion([Q0])});
            skCircle(sketch, "E197", {"center": v(15.32, -14.43) * mm, "radius": 17.5 * mm});
            skCircle(sketch, "E198.0", {"center": v(15.32, -14.43) * mm, "radius": 16 * mm});
            skSolve(sketch);
        }
        {
            var Q0;
            Q0=makeQuery(id+"F3.imprint","IMPRINT",FACE,{"disambiguationData":[TD([[makeQuery(id+"F3.imprint","IMPRINT",EDGE,{"derivedFrom":sQuery(id+"F3.wireOp",EDGE,"E197")}),1.0]])]});
            var Q1;
            Q1=makeQuery(id+"F3.imprint","IMPRINT",FACE,{"disambiguationData":[TD([[makeQuery(id+"F3.imprint","IMPRINT",EDGE,{"derivedFrom":sQuery(id+"F3.wireOp",EDGE,"E198.0")}),1.0]])]});
            extrude(context, id + "F4", {"entities" : qUnion([Q0, Q1]), "oppositeDirection" : true, "depth" : 1 * mm, "offsetDistance" : 25 * mm});
        }
        {
            var Q0;
            Q0=makeQuery(id+"F3.imprint","IMPRINT",FACE,{"disambiguationData":[TD([[makeQuery(id+"F3.imprint","IMPRINT",EDGE,{"derivedFrom":sQuery(id+"F3.wireOp",EDGE,"E197")}),1.0]])]});
            extrude(context, id + "F5", {"entities" : qUnion([Q0]), "operationType" : NewBodyOperationType.ADD, "depth" : 3 * mm, "offsetDistance" : 25 * mm});
        }
        {
            var Q0;
            Q0 = qSketchRegion(id + "F1", true);
            var Q1;
            Q1=makeQuery(id+"F1.imprint","IMPRINT",FACE,{"disambiguationData":[TD([[makeQuery(id+"F1.imprint","IMPRINT",EDGE,{"derivedFrom":sQuery(id+"F1.wireOp",EDGE,"E50.0.0")}),1.0]])]});
            extrude(context, id + "F6", {"entities" : qUnion([Q0, Q1]), "operationType" : NewBodyOperationType.ADD, "depth" : 2 * mm, "offsetDistance" : 25 * mm});
        }
        {
            var Q0;
            Q0=makeQuery(id+"F2.imprint","IMPRINT",FACE,{"disambiguationData":[TD([[makeQuery(id+"F2.imprint","IMPRINT",EDGE,{"derivedFrom":sQuery(id+"F2.wireOp",EDGE,"E169.0")}),-1.0]])]});
            var Q1;
            Q1=makeQuery(id+"F2.imprint","IMPRINT",FACE,{"disambiguationData":[TD([[makeQuery(id+"F2.imprint","IMPRINT",EDGE,{"derivedFrom":sQuery(id+"F2.wireOp",EDGE,"E148.0")}),1.0]])]});
            extrude(context, id + "F7", {"entities" : qUnion([Q0, Q1]), "operationType" : NewBodyOperationType.ADD, "depth" : 1 * mm, "offsetDistance" : 25 * mm});
        }
        {
            var Q0;
            Q0=makeQuery(id+"F6.opExtrude","CAP_FACE",FACE,{"disambiguationData":[OSD([sQuery(id+"F1.wireOp",EDGE,"E146"),sQuery(id+"F1.wireOp",EDGE,"E147.0.0"),sQuery(id+"F1.wireOp",EDGE,"E147.0.1"),sQuery(id+"F1.wireOp",EDGE,"E147.0.2"),sQuery(id+"F1.wireOp",EDGE,"E147.0.3"),sQuery(id+"F1.wireOp",EDGE,"E147.0.4"),sQuery(id+"F1.wireOp",EDGE,"E147.0.5"),sQuery(id+"F1.wireOp",EDGE,"E147.0.6"),sQuery(id+"F1.wireOp",EDGE,"E147.0.7"),sQuery(id+"F1.wireOp",EDGE,"E147.0.8"),sQuery(id+"F1.wireOp",EDGE,"E147.0.9"),sQuery(id+"F1.wireOp",EDGE,"E147.0.10"),sQuery(id+"F1.wireOp",EDGE,"E147.0.11"),sQuery(id+"F1.wireOp",EDGE,"E147.0.12"),sQuery(id+"F1.wireOp",EDGE,"E147.0.13"),sQuery(id+"F1.wireOp",EDGE,"E147.0.14"),sQuery(id+"F1.wireOp",EDGE,"E147.0.15"),sQuery(id+"F1.wireOp",EDGE,"E147.0.16"),sQuery(id+"F1.wireOp",EDGE,"E147.0.17"),sQuery(id+"F1.wireOp",EDGE,"E147.0.18"),sQuery(id+"F1.wireOp",EDGE,"E147.0.19"),sQuery(id+"F1.wireOp",EDGE,"E147.0.20"),sQuery(id+"F1.wireOp",EDGE,"E147.0.21"),sQuery(id+"F1.wireOp",EDGE,"E147.0.22"),sQuery(id+"F1.wireOp",EDGE,"E147.0.23"),sQuery(id+"F1.wireOp",EDGE,"E147.0.24"),sQuery(id+"F1.wireOp",EDGE,"E147.0.25"),sQuery(id+"F1.wireOp",EDGE,"E147.0.26"),sQuery(id+"F1.wireOp",EDGE,"E147.0.27"),sQuery(id+"F1.wireOp",EDGE,"E147.0.28"),sQuery(id+"F1.wireOp",EDGE,"E147.0.29"),sQuery(id+"F1.wireOp",EDGE,"E147.0.30"),sQuery(id+"F1.wireOp",EDGE,"E147.0.31")])],"isStart":false});
            var sketch = newSketch(context, id + "F8", { "sketchPlane" : qUnion([Q0])});
            skCircle(sketch, "E199", {"center": v(15.32, -0.6) * mm, "radius": 2.13 * mm});
            skSolve(sketch);
        }
        {
            var Q0;
            Q0 = qSketchRegion(id + "F8", true);
            extrude(context, id + "F9", {"entities" : qUnion([Q0]), "operationType" : NewBodyOperationType.REMOVE, "endBound" : BoundingType.THROUGH_ALL, "oppositeDirection" : true, "depth" : 25 * mm, "offsetDistance" : 25 * mm});
        }
    });
